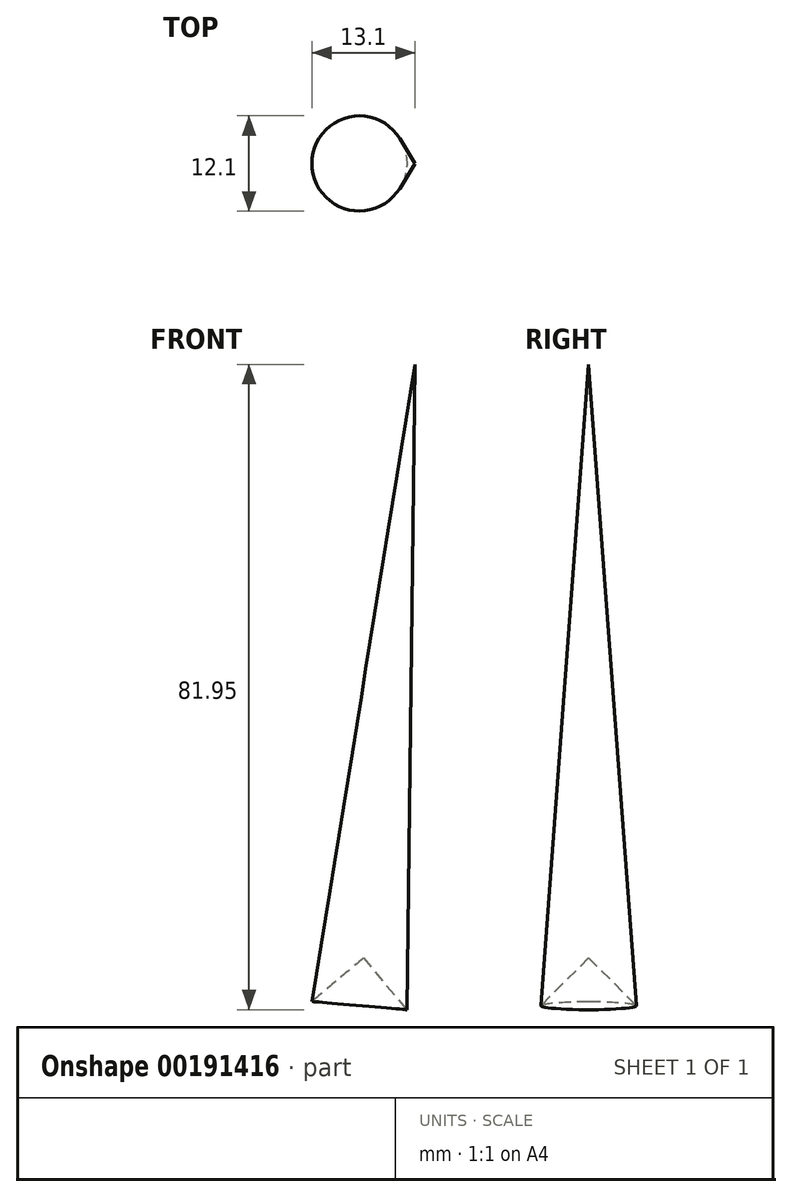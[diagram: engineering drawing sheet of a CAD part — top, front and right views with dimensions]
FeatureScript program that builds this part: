
annotation { "Feature Type Name" : "Feature", "Feature Type Description" : "" }
export const myFeature = defineFeature(function(context is Context, id is Id, definition is map)
    precondition{}
    {
        {
            var Q0;
            Q0=qCreatedBy(makeId("Front.planeOp"),FACE);
            var sketch = newSketch(context, id + "F0", { "sketchPlane" : qUnion([Q0])});
            skLineSegment(sketch, "E0", {"start": v(0, 60.23) * mm, "end": v(-13.1, -20.68) * mm});
            skLineSegment(sketch, "E1", {"start": v(-6.55, -15.15) * mm, "end": v(0, 60.23) * mm});
            skLineSegment(sketch, "E2", {"start": v(-6.55, -15.15) * mm, "end": v(-13.1, -20.68) * mm});
            skLineSegment(sketch, "E3", {"start": v(0, 60.23) * mm, "end": v(0, -20.68) * mm});
            skLineSegment(sketch, "E4", {"start": v(-6.55, -15.15) * mm, "end": v(0, -20.68) * mm});
            skSolve(sketch);
        }
        {
            var Q0;
            Q0=makeQuery(id+"F0.imprint","IMPRINT",FACE,{"disambiguationData":[TD([[makeQuery(id+"F0.imprint","IMPRINT",EDGE,{"derivedFrom":sQuery(id+"F0.wireOp",EDGE,"E0")}),1.0]])]});
            var Q1;
            Q1=sQuery(id+"F0.wireOp",EDGE,"E1");
            revolve(context, id + "F1", {"entities" : qUnion([Q0]), "axis" : qUnion([Q1]), "revolveType" : RevolveType.FULL});
        }
    });
